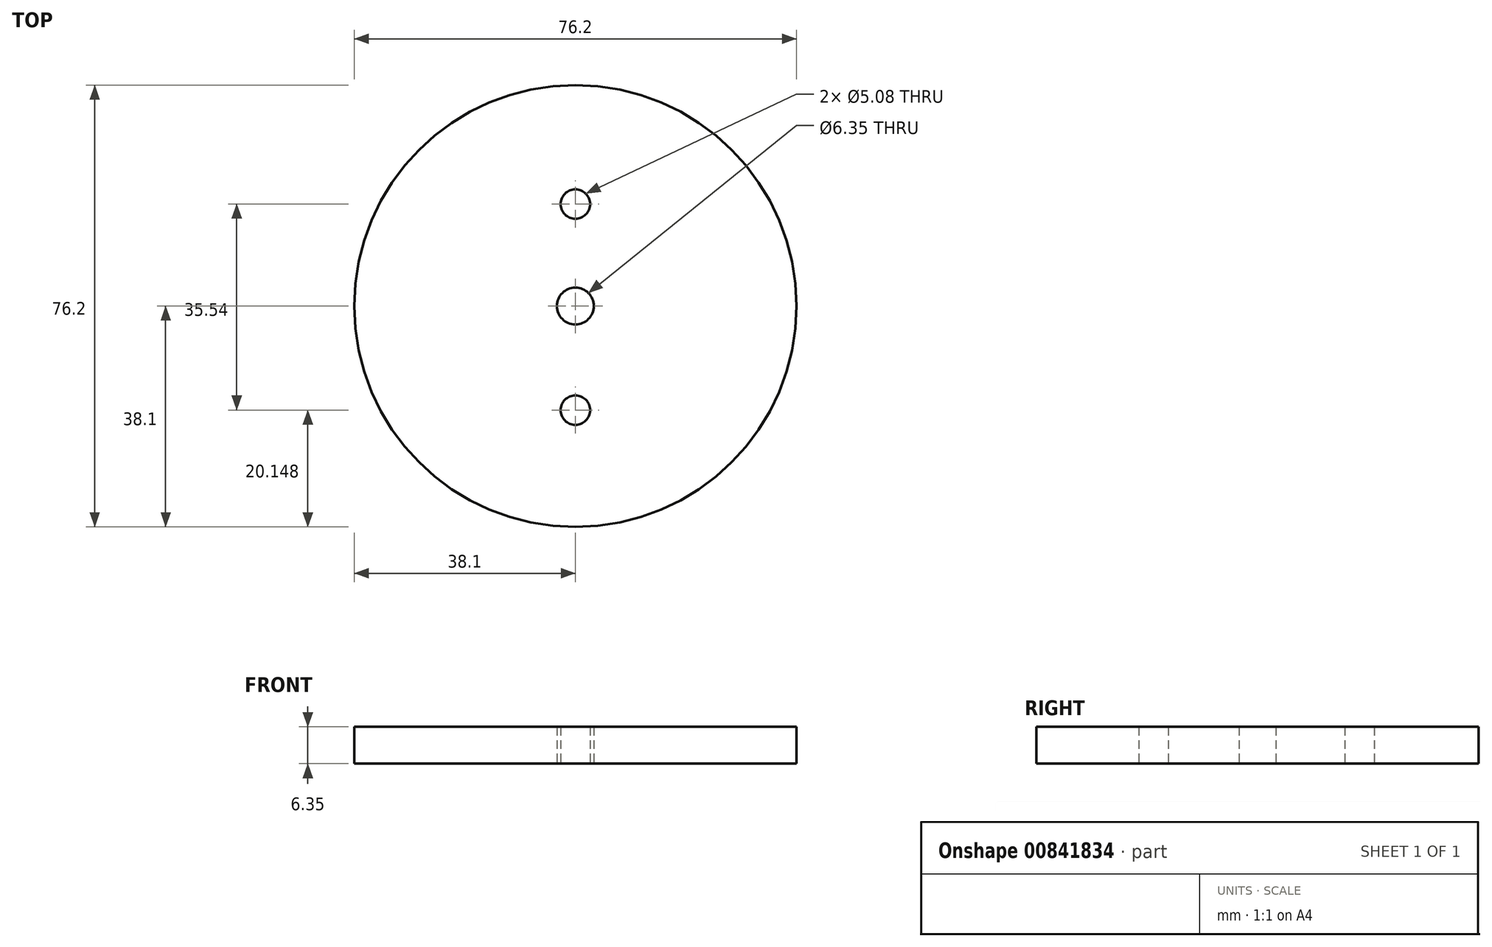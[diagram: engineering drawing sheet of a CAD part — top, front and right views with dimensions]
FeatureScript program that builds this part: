
annotation { "Feature Type Name" : "Feature", "Feature Type Description" : "" }
export const myFeature = defineFeature(function(context is Context, id is Id, definition is map)
    precondition{}
    {
        {
            var Q0;
            Q0=qCreatedBy(makeId("Top.planeOp"),FACE);
            var sketch = newSketch(context, id + "F0", { "sketchPlane" : qUnion([Q0])});
            skCircle(sketch, "E0", {"center": v(0, 0) * mm, "radius": 38.1 * mm});
            skCircle(sketch, "E1", {"center": v(0, 0) * mm, "radius": 3.18 * mm});
            skCircle(sketch, "E2", {"center": v(0, 17.59) * mm, "radius": 2.54 * mm});
            skCircle(sketch, "E3", {"center": v(0, -17.95) * mm, "radius": 2.54 * mm});
            skSolve(sketch);
        }
        {
            var Q0;
            Q0=makeQuery(id+"F0.imprint","IMPRINT",FACE,{"disambiguationData":[TD([[makeQuery(id+"F0.imprint","IMPRINT",EDGE,{"derivedFrom":sQuery(id+"F0.wireOp",EDGE,"E0")}),1.0]])]});
            extrude(context, id + "F1", {"entities" : qUnion([Q0]), "depth" : 6.35 * mm, "offsetDistance" : 25.4 * mm});
        }
    });
